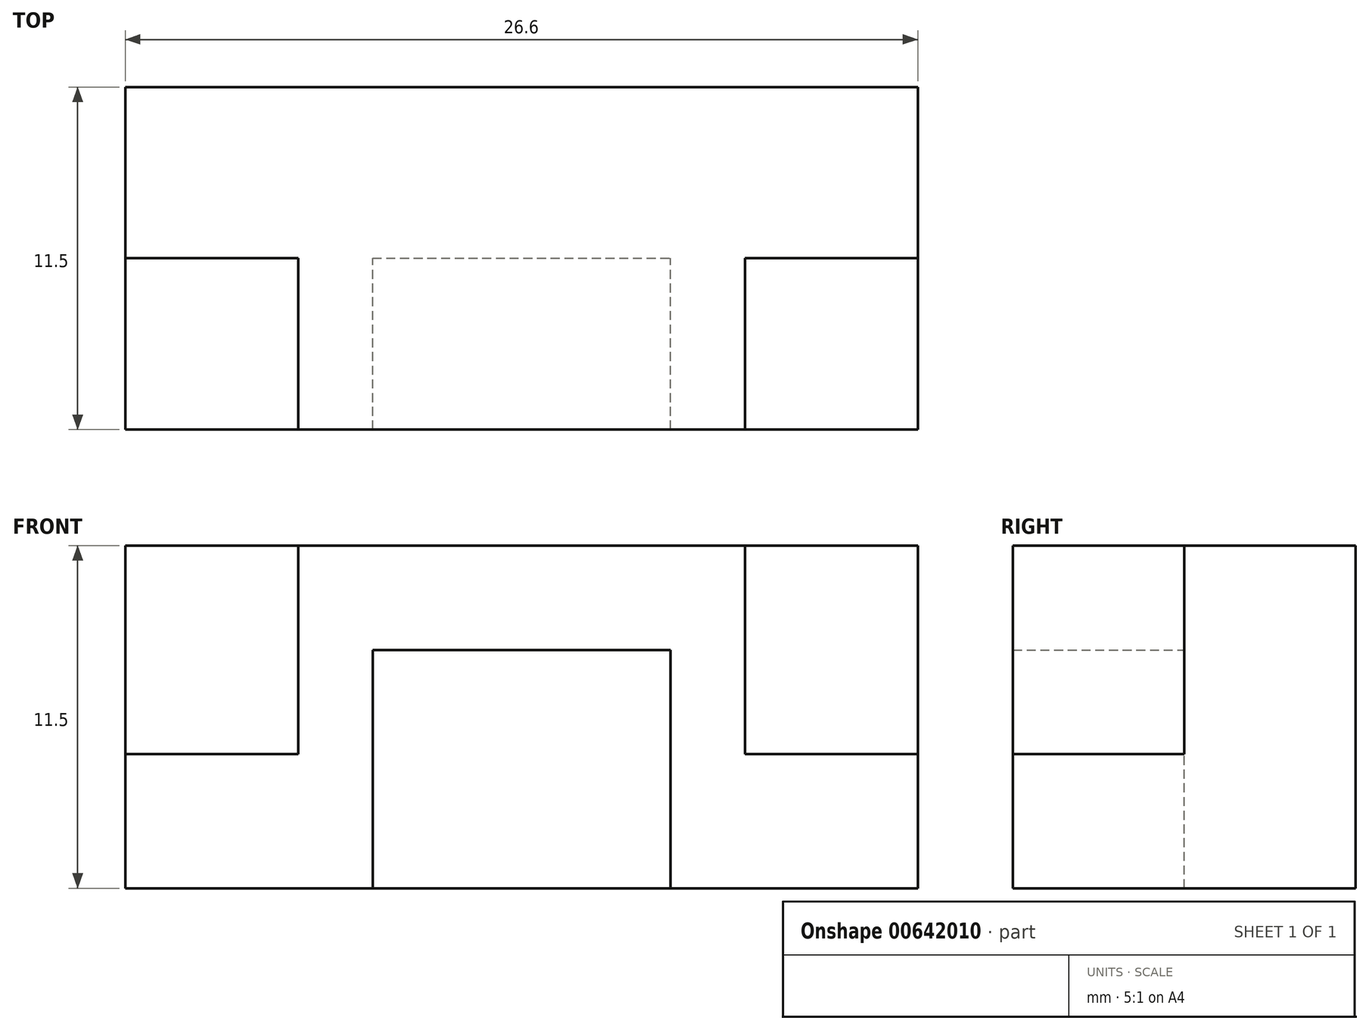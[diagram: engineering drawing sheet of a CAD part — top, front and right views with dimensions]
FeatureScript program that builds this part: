
annotation { "Feature Type Name" : "Feature", "Feature Type Description" : "" }
export const myFeature = defineFeature(function(context is Context, id is Id, definition is map)
    precondition{}
    {
        {
            var Q0;
            Q0=qCreatedBy(makeId("Top.planeOp"),FACE);
            var sketch = newSketch(context, id + "F0", { "sketchPlane" : qUnion([Q0])});
            skLineSegment(sketch, "E0.bottom", {"start": v(-13.3, 5.75) * mm, "end": v(13.3, 5.75) * mm});
            skLineSegment(sketch, "E0.top", {"start": v(-13.3, -5.75) * mm, "end": v(13.3, -5.75) * mm});
            skLineSegment(sketch, "E0.left", {"start": v(-13.3, 5.75) * mm, "end": v(-13.3, -5.75) * mm});
            skLineSegment(sketch, "E0.right", {"start": v(13.3, 5.75) * mm, "end": v(13.3, -5.75) * mm});
            skPoint(sketch, "E1", {"position": v(0, 5.75) * mm});
            skPoint(sketch, "E2", {"position": v(13.3, 0) * mm});
            skPoint(sketch, "E3", {"position": v(0, -5.75) * mm});
            skSolve(sketch);
        }
        {
            var Q0;
            Q0 = qSketchRegion(id + "F0", true);
            extrude(context, id + "F1", {"entities" : qUnion([Q0]), "depth" : 11.5 * mm, "offsetDistance" : 25 * mm});
        }
        {
            var Q0;
            Q0=qCreatedBy(makeId("Front.planeOp"),FACE);
            var sketch = newSketch(context, id + "F2", { "sketchPlane" : qUnion([Q0])});
            skLineSegment(sketch, "E4.bottom", {"start": v(-13.3, 11.5) * mm, "end": v(-7.5, 11.5) * mm});
            skLineSegment(sketch, "E4.top", {"start": v(-13.3, 4.5) * mm, "end": v(-7.5, 4.5) * mm});
            skLineSegment(sketch, "E4.left", {"start": v(-13.3, 11.5) * mm, "end": v(-13.3, 4.5) * mm});
            skLineSegment(sketch, "E4.right", {"start": v(-7.5, 11.5) * mm, "end": v(-7.5, 4.5) * mm});
            skLineSegment(sketch, "E5.bottom", {"start": v(13.3, 11.5) * mm, "end": v(7.5, 11.5) * mm});
            skLineSegment(sketch, "E5.top", {"start": v(13.3, 4.5) * mm, "end": v(7.5, 4.5) * mm});
            skLineSegment(sketch, "E5.left", {"start": v(13.3, 11.5) * mm, "end": v(13.3, 4.5) * mm});
            skLineSegment(sketch, "E5.right", {"start": v(7.5, 11.5) * mm, "end": v(7.5, 4.5) * mm});
            skLineSegment(sketch, "E6.bottom", {"start": v(-5, 0) * mm, "end": v(5, 0) * mm});
            skLineSegment(sketch, "E6.top", {"start": v(-5, 8) * mm, "end": v(5, 8) * mm});
            skLineSegment(sketch, "E6.left", {"start": v(-5, 0) * mm, "end": v(-5, 8) * mm});
            skLineSegment(sketch, "E6.right", {"start": v(5, 0) * mm, "end": v(5, 8) * mm});
            skPoint(sketch, "E7", {"position": v(0, 8) * mm});
            skSolve(sketch);
        }
        {
            var Q0;
            Q0 = qSketchRegion(id + "F2", true);
            extrude(context, id + "F3", {"entities" : qUnion([Q0]), "operationType" : NewBodyOperationType.REMOVE, "endBound" : BoundingType.THROUGH_ALL, "depth" : 6.6 * mm, "offsetDistance" : 25 * mm});
        }
    });
